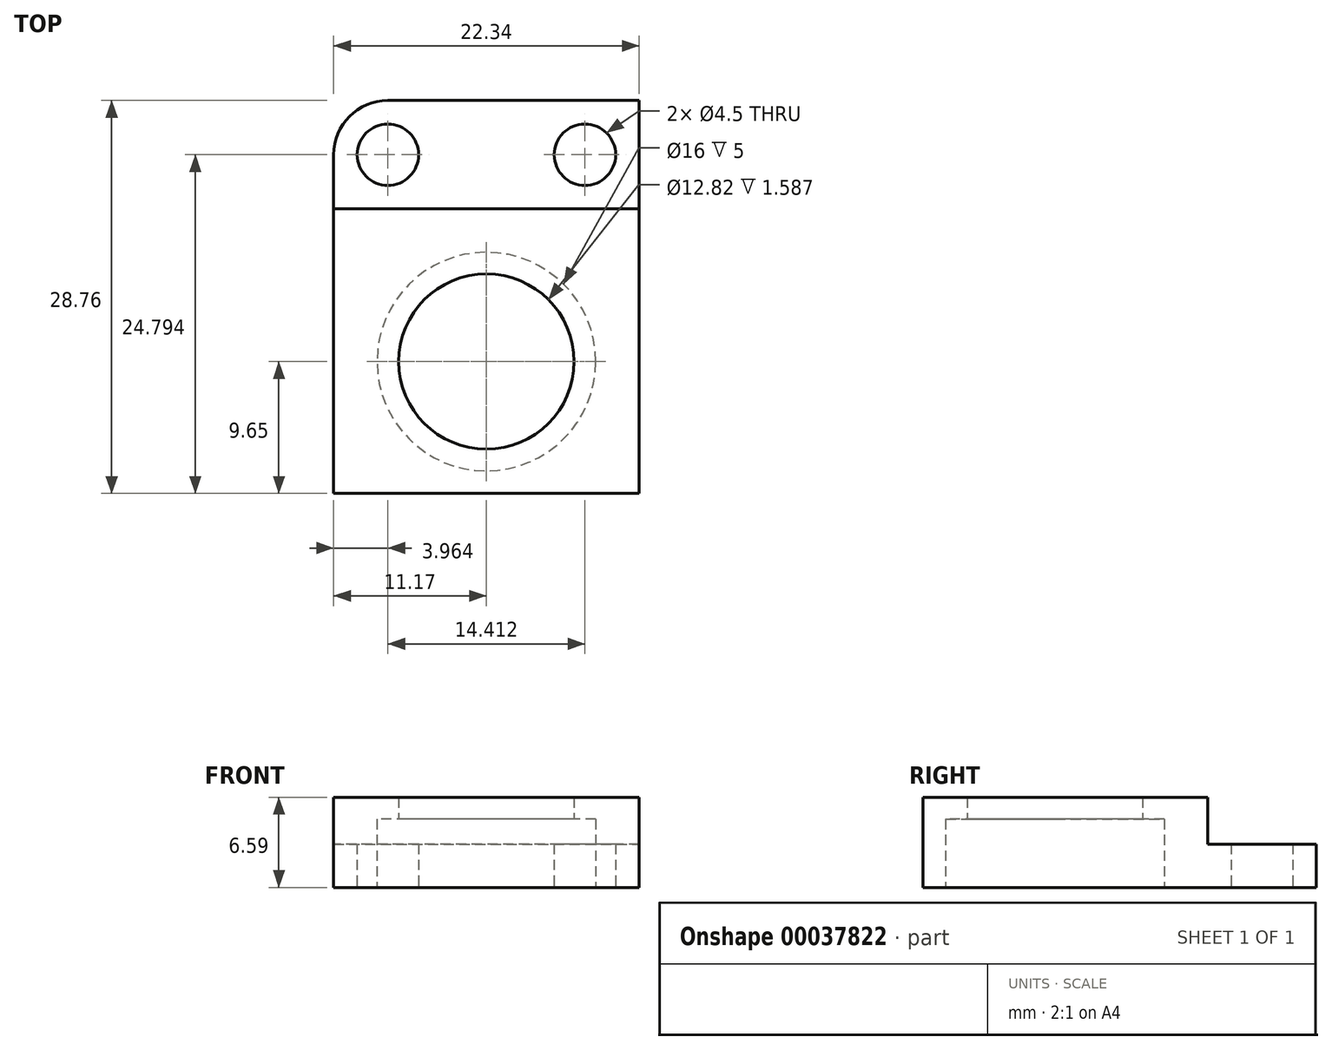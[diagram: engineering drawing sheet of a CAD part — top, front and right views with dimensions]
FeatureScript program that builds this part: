
annotation { "Feature Type Name" : "Feature", "Feature Type Description" : "" }
export const myFeature = defineFeature(function(context is Context, id is Id, definition is map)
    precondition{}
    {
        {
            var Q0;
            Q0=qCreatedBy(makeId("Top.planeOp"),FACE);
            var sketch = newSketch(context, id + "F0", { "sketchPlane" : qUnion([Q0])});
            skLineSegment(sketch, "E0", {"start": v(0, 0) * mm, "end": v(0, 9.65) * mm, "construction": true});
            skLineSegment(sketch, "E1", {"start": v(0, 9.65) * mm, "end": v(0, 28.76) * mm, "construction": true});
            skLineSegment(sketch, "E2", {"start": v(11.17, 0) * mm, "end": v(-11.17, 0) * mm});
            skLineSegment(sketch, "E3", {"start": v(-11.17, 0) * mm, "end": v(-11.17, 28.76) * mm});
            skLineSegment(sketch, "E4", {"start": v(11.17, 0) * mm, "end": v(11.17, 28.76) * mm});
            skLineSegment(sketch, "E5", {"start": v(11.17, 28.76) * mm, "end": v(-11.17, 28.76) * mm});
            skCircle(sketch, "E6", {"center": v(7.2, 24.8) * mm, "radius": 3.97 * mm, "construction": true});
            skLineSegment(sketch, "E7", {"start": v(7.2, 24.8) * mm, "end": v(-7.2, 24.8) * mm, "construction": true});
            skPoint(sketch, "E8", {"position": v(0, 24.8) * mm});
            skCircle(sketch, "E9", {"center": v(-7.2, 24.8) * mm, "radius": 2.25 * mm});
            skCircle(sketch, "E10", {"center": v(7.2, 24.8) * mm, "radius": 2.25 * mm});
            skCircle(sketch, "E11", {"center": v(0, 9.65) * mm, "radius": 8 * mm});
            skSolve(sketch);
        }
        {
            var Q0;
            Q0 = qSketchRegion(id + "F0", true);
            extrude(context, id + "F1", {"entities" : qUnion([Q0]), "depth" : 3.17 * mm});
        }
        {
            var Q0;
            Q0=makeQuery(id+"F1.opExtrude","CAP_FACE",FACE,{"disambiguationData":[OSD([sQuery(id+"F0.wireOp",EDGE,"cd2821f5-4831-4a1e-b02c-f6531e8d6a60"),sQuery(id+"F0.wireOp",EDGE,"f5fb9684-6b33-4355-9c5c-313f103c1c62"),sQuery(id+"F0.wireOp",EDGE,"ad4d735d-fb8e-4b7d-bd62-e2e4cd1506b4"),sQuery(id+"F0.wireOp",EDGE,"E2"),sQuery(id+"F0.wireOp",EDGE,"E3"),sQuery(id+"F0.wireOp",EDGE,"1d698fc5-a467-472c-b147-6fd77103e892"),sQuery(id+"F0.wireOp",EDGE,"E4"),sQuery(id+"F0.wireOp",EDGE,"E5"),sQuery(id+"F0.wireOp",EDGE,"E9"),sQuery(id+"F0.wireOp",EDGE,"E10")])],"isStart":false});
            var sketch = newSketch(context, id + "F2", { "sketchPlane" : qUnion([Q0])});
            skLineSegment(sketch, "E12.bottom", {"start": v(-11.17, 0) * mm, "end": v(11.17, 0) * mm});
            skLineSegment(sketch, "E12.top", {"start": v(-11.17, 20.83) * mm, "end": v(11.17, 20.83) * mm});
            skLineSegment(sketch, "E12.left", {"start": v(-11.17, 0) * mm, "end": v(-11.17, 20.83) * mm});
            skLineSegment(sketch, "E12.right", {"start": v(11.17, 0) * mm, "end": v(11.17, 20.83) * mm});
            skCircle(sketch, "E13", {"center": v(0, 9.65) * mm, "radius": 8 * mm});
            skSolve(sketch);
        }
        {
            var Q0;
            Q0 = qSketchRegion(id + "F2", true);
            extrude(context, id + "F3", {"entities" : qUnion([Q0]), "operationType" : NewBodyOperationType.ADD, "depth" : 1.82 * mm});
        }
        {
            var Q0;
            Q0=makeQuery(id+"F3.opExtrude","CAP_FACE",FACE,{"disambiguationData":[OSD([sQuery(id+"F2.wireOp",EDGE,"E12.bottom"),sQuery(id+"F2.wireOp",EDGE,"E12.top"),sQuery(id+"F2.wireOp",EDGE,"E12.left"),sQuery(id+"F2.wireOp",EDGE,"E12.right"),sQuery(id+"F2.wireOp",EDGE,"E13")])],"isStart":false});
            var sketch = newSketch(context, id + "F4", { "sketchPlane" : qUnion([Q0])});
            skCircle(sketch, "E14", {"center": v(0, 9.65) * mm, "radius": 6.41 * mm});
            skLineSegment(sketch, "E15.bottom", {"start": v(-11.17, 0) * mm, "end": v(11.17, 0) * mm});
            skLineSegment(sketch, "E15.top", {"start": v(-11.17, 20.83) * mm, "end": v(11.17, 20.83) * mm});
            skLineSegment(sketch, "E15.left", {"start": v(-11.17, 0) * mm, "end": v(-11.17, 20.83) * mm});
            skLineSegment(sketch, "E15.right", {"start": v(11.17, 0) * mm, "end": v(11.17, 20.83) * mm});
            skSolve(sketch);
        }
        {
            var Q0;
            Q0=makeQuery(id+"F4.imprint","IMPRINT",FACE,{"disambiguationData":[TD([[makeQuery(id+"F4.imprint","IMPRINT",EDGE,{"derivedFrom":sQuery(id+"F4.wireOp",EDGE,"E15.top")}),-1.0]])]});
            var Q1;
            Q1=makeQuery(id+"F4.imprint","IMPRINT",FACE,{"disambiguationData":[TD([[makeQuery(id+"F4.imprint","IMPRINT",EDGE,{"derivedFrom":sQuery(id+"F4.wireOp",EDGE,"E14")}),-1.0]])]});
            extrude(context, id + "F5", {"entities" : qUnion([Q0, Q1]), "operationType" : NewBodyOperationType.ADD, "depth" : 1.59 * mm});
        }
        {
            var Q0;
            Q0=makeQuery(id+"F1.opExtrude","SWEPT_EDGE",EDGE,{"disambiguationData":[OSD([sQuery(id+"F0.wireOp",EDGE,"E3"),sQuery(id+"F0.wireOp",EDGE,"E5")])]});
            fillet(context, id + "F6", {"entities" : qUnion([Q0]), "radius" : 3.97 * mm, "tangentPropagation" : true, "allowEdgeOverflow" : false});
        }
    });
